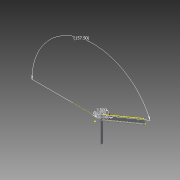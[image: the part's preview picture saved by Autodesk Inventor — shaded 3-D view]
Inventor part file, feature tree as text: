
AUTODESK INVENTOR PART (.ipt)
format: ipt  version: 2013 (Build 170138000, 138)  size: 183,296 bytes
history: native  units: in
note: dims shown in document units (in); Inventor stores cm internally (conversion verified against a paired STEP export)
features: sketch x5, extrude x4, hole x2, plane x1
ambient origin geometry x8: Origin, YZ Plane, XZ Plane, XY Plane, X Axis, Y Axis, Z Axis, Center Point
bodies: Solid1 (feature_tree)
feature tree (12):
  plane  "Work Plane1"
  extrude  "Extrusion1"  Depth=19.0in
  extrude  "Extrusion2"  TaperAngle=90.0deg  [1 undecoded]
  extrude  "Extrusion3"  TaperAngle=90.0deg  [1 undecoded]
  extrude  "Extrusion4"  TaperAngle=90.0deg  [1 undecoded]
  sketch  "Sketch9"  dims[d8=53.0in d9=90.0deg d10=21.0in d11=7.0in d12=0.5in d14=2.5in d15=0.5in d16=0.75in d17=22.5deg d18=0.5in d19=90.0deg d20=90.0deg d21=0.5in d22=112.5deg d23=23.2731in d24=90.0deg d25=10.0in d26=90.0deg d27=1.0in d28=90.0deg d29=90.0deg d30=1.0in d31=0.0in d32=22.5deg d33=1.0in d34=112.5deg d35=2.0in d36=0.0in d39=1.0in d40=2.0in d42=157.5deg d43=1.0in d44=0.0in d59=1.0in d60=0.0in d61=0.125in d62=180.0deg d63=0.125in d64=112.5deg d65=90.0deg d66=0.875in d67=0.0in d85=10.0in d86=157.5deg d89=0.5in d91=3.5in d92=0.25in d93=0.75in d94=0.375in d95=0.25in d96=0.5635in d97=1.0in d98=0.8108in d100=0.75in d101=0.25in d102=0.75in d103=0.375in d104=0.25in d105=0.5635in d106=1.0in d107=0.8108in]
  hole  "Hole2"  [1 undecoded]
  hole  "Hole3"  [1 undecoded]
  sketch  "Sketch1"  dims[d0=2.5in d1=19.0in]
  sketch  "Sketch2"  dims[d2=3.0in d3=90.0deg]
  sketch  "Sketch4"  dims[d4=5.0in d5=90.0deg]
  sketch  "Sketch5"  dims[d6=4.0in d7=90.0deg]
note: 5 required parameter values undecoded (feature->parameter linkage not recoverable at this tier; creation-order binding heuristic only, values carry confidence <= 0.55)
